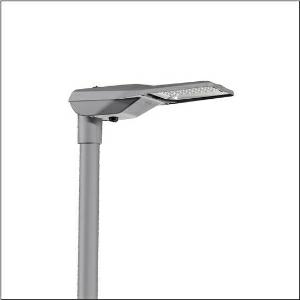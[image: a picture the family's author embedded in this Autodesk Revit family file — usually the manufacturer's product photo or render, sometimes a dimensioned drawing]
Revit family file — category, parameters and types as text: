
# Revit family: streetlight_sl_21_iq_mini___st0_5a_5xe2b31y08hb_0ff0
name_source: partatom
category: Lighting Fixtures
units: mm (PartAtom-declared; Revit-internal decimal feet)

## family parameters
Cut with Voids When Loaded = No
Host = Face
Light Source = No
Part Type = Normal
Room Calculation Point = No
Round Connector Dimension = Use Diameter
Shared = No

## types (1)
- --- (1 x LED, 9750 lm, 71 W, 3000K)
    Apparent Load = 71 VA
    CIE Flux Codes = 41 75 97 100 100
    Color Rendering = 70
    Color Temperature = 3000K
    Default Elevation = 1800 mm
    Description = Streetlight SL 21 iQ mini, mast luminaire, primary light control with lens, of PMMA, primary optical cover: cover, of toughened safety glass, transparent, light distribution: ST0.5a, light emission: direct distribution, primary light characteristic: asymmetric, installation type: post-top, side-entry, LED, High Power LED, rated luminous flux: 9.750lm, luminous efficacy: 137lm/W, light colour: 730, colour temperature: 3000K, control gear: iQ-Street Remote, D4i with power reduction, control: pre-setting: logarithmic dimming characteristic, Street-Remote, Auto-Match, Temp-Guard, Lumen-Switch, Night-Set, Smart-Wire, Light-Fading, Desk-Remote (wireless, voltage-free reading and setting of iQ features in the workshop via application-optimized NFC function/RFID function), optimised constant luminous flux control (CLO 2.0), mains connection: 220..240V, AC, 50/60Hz, start of lifetime: 71W, end of service life: 75W, reduction: 30W, luminaire housing, of diecast aluminium, powder-coated, Siteco® metallic grey (DB 702S), corrosivity category C5 mid according to DIN EN ISO 12944, please order mast flange separately, inclination adjustable: 0°, 5°, 10°, 15°, sealing non-destructively replaceable, multi-level sealing system, length: 628mm, width: 235mm, height: 110mm, mast flange for spigot size: 42mm (side-entry): 5XC10008XM4, 60/48mm (side-entry/post-top): 5XC10108XM2, 76/60mm (side-entry/post-top): 5XC10108XM1, mounting height: 4..8m, Smart Interface below and above, protection rating (complete): IP66, insulation class (complete): insulation class II (safety insulation), certification: CE, ENEC, ENEC+, VDE, impact resistance: IK10, permissible operating ambient temperature for outdoor applications: -40..+50°C, standard-compliant lighting for roads and squares, packaging unit: 1 piece

Light Distribution: ST0.5a
    Height = 110 mm
    Lamp = 1 x LED
    Lamp Light Flux = 9750 lm
    Lamp Power = 71 W
    Lamp count = 1
    Length = 625 mm
    Luminous efficacy = 137 lm/W
    Manufacturer = Siteco
    ModVariant = No
    Model = 5XE2B31Y08HB
    Number of Poles = 1
    OnlyDefault = Yes
    Power Factor = 1
    Product Name = Streetlight SL 21 iQ mini | ST0.5a
    Product group = mast luminaire | pylon top
    ProductGroupID = 6100
    Protection Class = Protection class II
    Protection Degree = IP 66
    RLX_Detail_Level = 1
    RLX_Emergency_Light_Flux = 0 lm
    RLX_Emergency_Type = 0
    RLX_Emergency_Type_DB = No
    RlxData = <blob elided: 37617 chars, md5=6c83aa8b>
    Socket = socket
    Standby Power = 0 W
    System Light Flux = 9750 lm
    System Power = 71 W
    Type Comments = factory setting: luminous flux: 100 % | dim-lin: 254 | 716 mA
    Type Image = l_1003514.jpg
    URL = http://relux.com
    VarID = @adj_116104
    Voltage = 0 V
    Weight = 0.00 kg
    Width = 234 mm

## geometry (parser evidence)
native form markers: Blend x4, Sweep x11
no freeform markers — native parametric forms only
